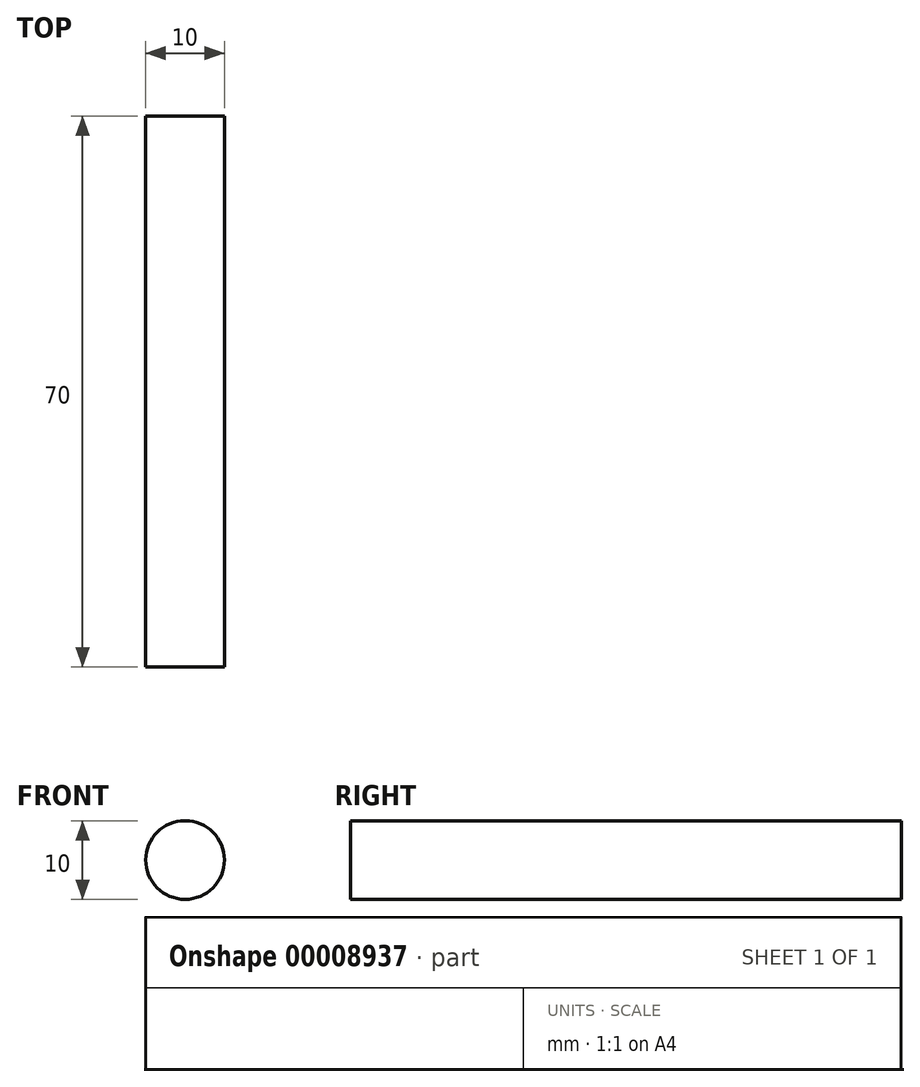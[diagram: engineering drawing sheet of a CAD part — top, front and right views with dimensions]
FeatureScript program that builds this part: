
annotation { "Feature Type Name" : "Feature", "Feature Type Description" : "" }
export const myFeature = defineFeature(function(context is Context, id is Id, definition is map)
    precondition{}
    {
        {
            var Q0;
            Q0=qCreatedBy(makeId("Front.planeOp"),FACE);
            var sketch = newSketch(context, id + "F0", { "sketchPlane" : qUnion([Q0])});
            skCircle(sketch, "E0", {"center": v(0, 0) * mm, "radius": 5 * mm});
            skLineSegment(sketch, "E1", {"start": v(0, 0) * mm, "end": v(5, 0) * mm});
            skSolve(sketch);
        }
        {
            var Q0;
            Q0 = qSketchRegion(id + "F0", true);
            extrude(context, id + "F1", {"entities" : qUnion([Q0]), "depth" : 35 * mm, "hasSecondDirection" : true, "secondDirectionOppositeDirection" : true, "secondDirectionDepth" : 35 * mm});
        }
    });
